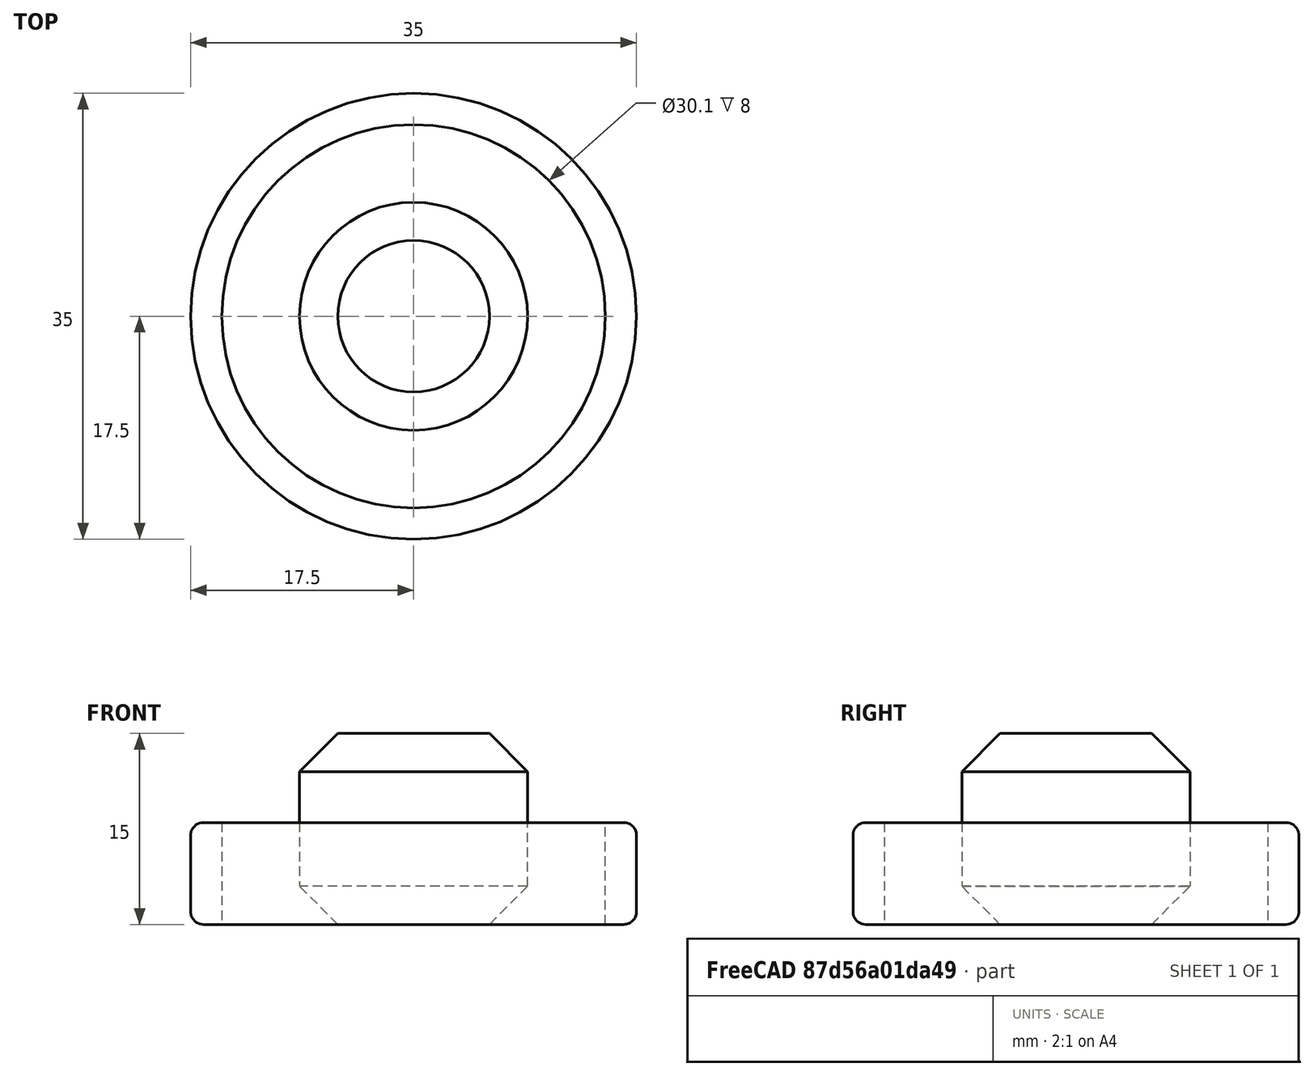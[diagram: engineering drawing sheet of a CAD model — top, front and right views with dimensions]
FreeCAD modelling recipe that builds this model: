
FCSTD DOCUMENT  (FreeCAD 0.18R16146 (Git))
Label: b4
License: All rights reserved
LicenseURL: http://en.wikipedia.org/wiki/All_rights_reserved
objects: Sketcher::SketchObject×2, PartDesign::Pad×2, PartDesign::Body×2, PartDesign::Fillet×1, PartDesign::Chamfer×1
note: 10 computed .brp shape members not serialized (recipe doc carries the construction recipe); baked Part::Feature solids carry a one-line shape summary decoded from their .brp

FEATURE [Sketcher::SketchObject] Sketch
  MapMode = 5
  Support = -> [XY_Plane]
  sketch-geometry (2):
    g0: Circle CenterX=0 CenterY=0 CenterZ=0 NormalX=0 NormalY=0 NormalZ=1 AngleXU=0 Radius=15.05
    g1: Circle CenterX=0 CenterY=0 CenterZ=0 NormalX=0 NormalY=0 NormalZ=1 AngleXU=0 Radius=17.5
  constraints (3):
    c: PointOnObject(g1,g-1)
    c: Diameter(g0) = 30.1
    c: Diameter(g1) = 35
FEATURE [Sketcher::SketchObject] Sketch001
  MapMode = 5
  sketch-geometry (1):
    g0: Circle CenterX=0 CenterY=0 CenterZ=0 NormalX=0 NormalY=0 NormalZ=1 AngleXU=0 Radius=8.95
  constraints (2):
    c: PointOnObject(g0,g-1)
    c: Diameter(g0) = 17.9
FEATURE [PartDesign::Pad] Pad
  Length = 8
  Length2 = 100
  Profile = -> Sketch
  Type = 0
FEATURE [PartDesign::Pad] Pad001
  Length = 15
  Length2 = 100
  Profile = -> Sketch001
  Type = 0
FEATURE [PartDesign::Fillet] Fillet
  Base = -> Pad [Face1]
  BaseFeature = -> Pad
  Radius = 1
FEATURE [PartDesign::Body] Body  label="ring"
  Group = -> [Sketch,Pad,Fillet]
  Origin = -> Origin
  Tip = -> Fillet
FEATURE [PartDesign::Chamfer] Chamfer
  Base = -> Pad001 [Face1]
  BaseFeature = -> Pad001
  Size = 3
FEATURE [PartDesign::Body] Body001  label="hub"
  Group = -> [Sketch001,Pad001,Chamfer]
  Origin = -> Origin001
  Tip = -> Chamfer
